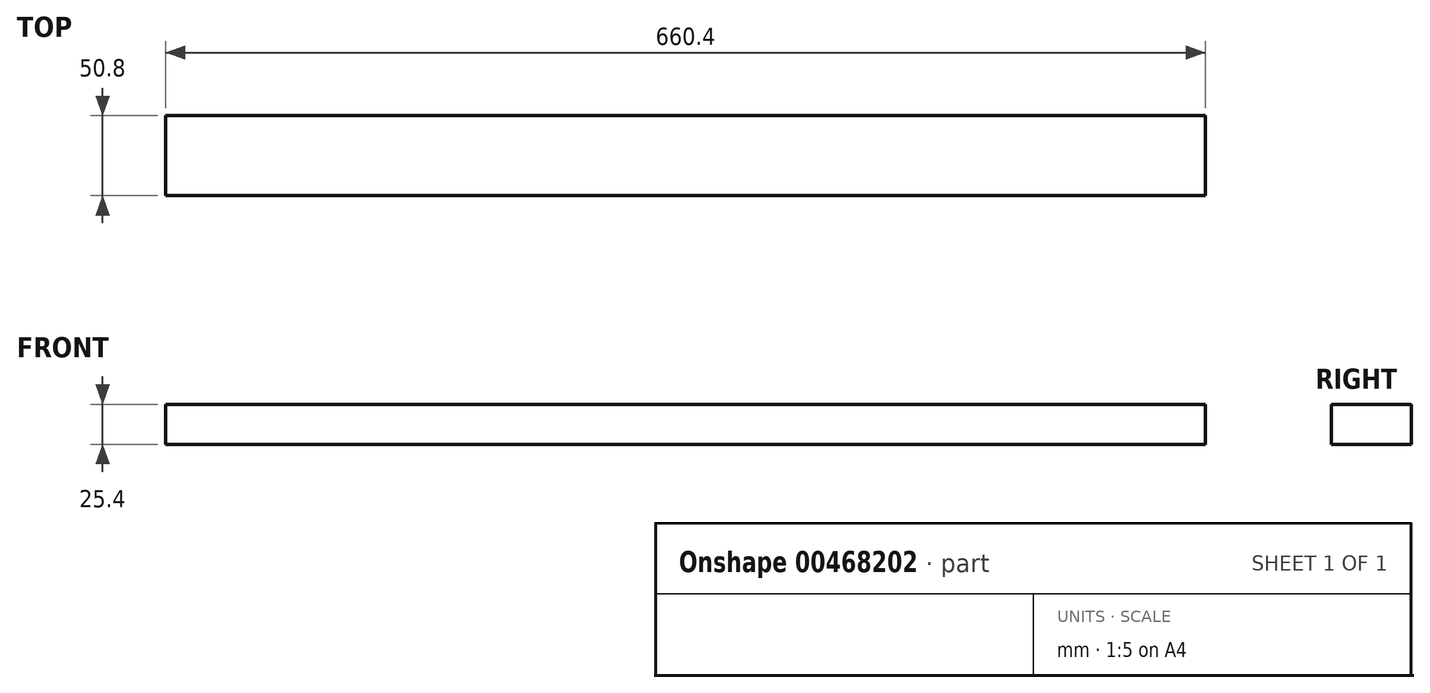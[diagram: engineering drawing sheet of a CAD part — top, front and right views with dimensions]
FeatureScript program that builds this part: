
annotation { "Feature Type Name" : "Feature", "Feature Type Description" : "" }
export const myFeature = defineFeature(function(context is Context, id is Id, definition is map)
    precondition{}
    {
        {
            var Q0;
            Q0=qCreatedBy(makeId("Top.planeOp"),FACE);
            var sketch = newSketch(context, id + "F0", { "sketchPlane" : qUnion([Q0])});
            skLineSegment(sketch, "E0.bottom", {"start": v(0, 0) * mm, "end": v(660.4, 0) * mm});
            skLineSegment(sketch, "E0.top", {"start": v(0, 50.8) * mm, "end": v(660.4, 50.8) * mm});
            skLineSegment(sketch, "E0.left", {"start": v(0, 0) * mm, "end": v(0, 50.8) * mm});
            skLineSegment(sketch, "E0.right", {"start": v(660.4, 0) * mm, "end": v(660.4, 50.8) * mm});
            skSolve(sketch);
        }
        {
            var Q0;
            Q0=makeQuery(id+"F0.imprint","IMPRINT",FACE,{"disambiguationData":[TD([[makeQuery(id+"F0.imprint","IMPRINT",EDGE,{"derivedFrom":sQuery(id+"F0.wireOp",EDGE,"E0.bottom")}),1.0]])]});
            extrude(context, id + "F1", {"entities" : qUnion([Q0]), "depth" : 25.4 * mm, "offsetDistance" : 25.4 * mm});
        }
    });
